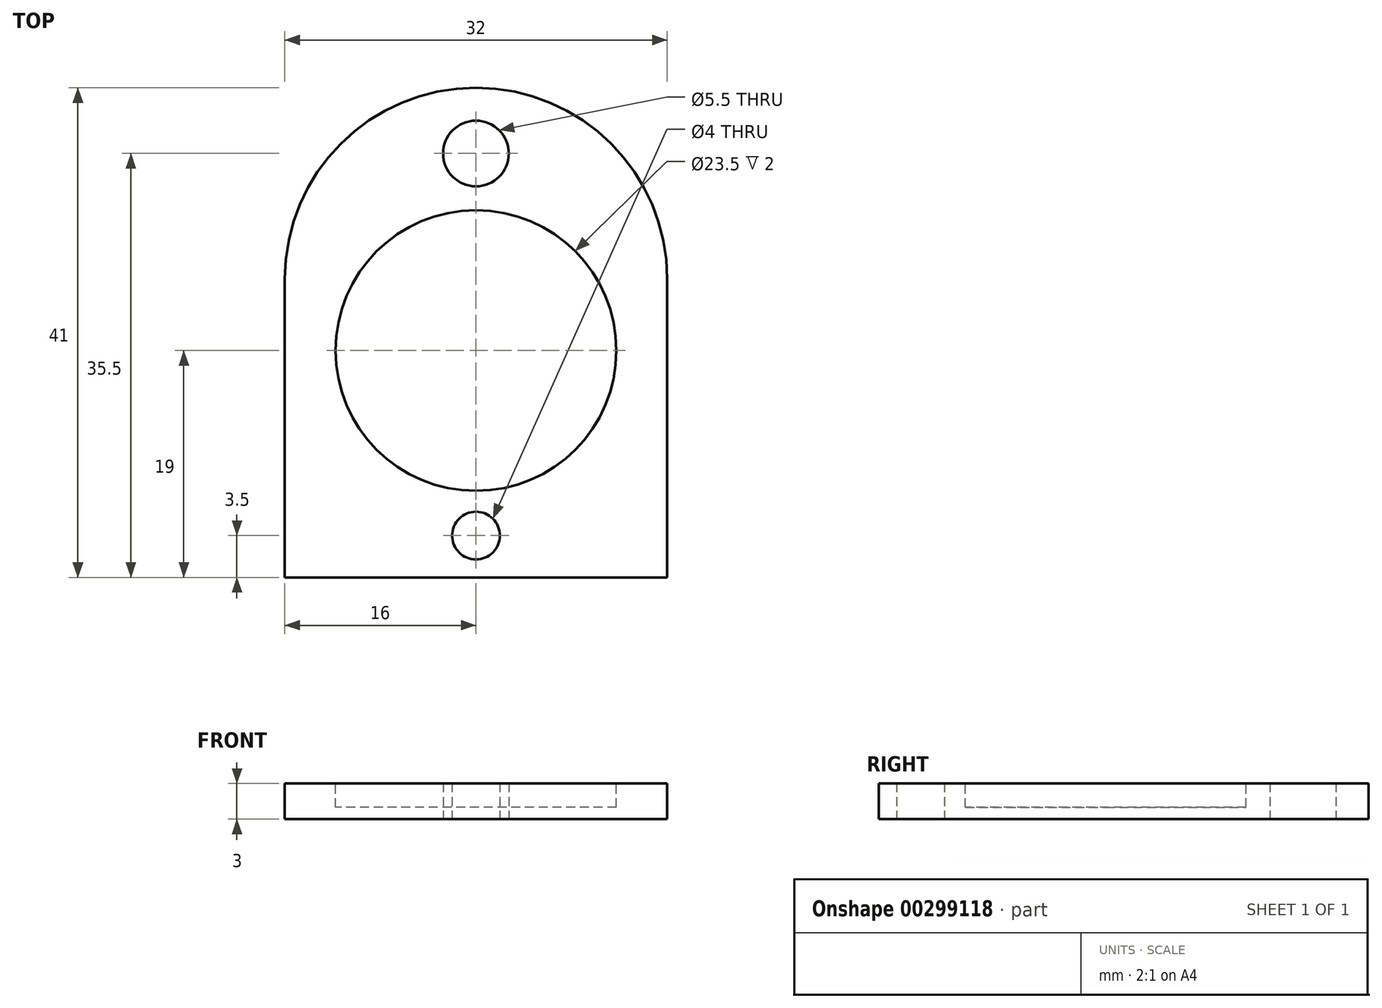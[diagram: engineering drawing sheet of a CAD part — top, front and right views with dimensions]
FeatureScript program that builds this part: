
annotation { "Feature Type Name" : "Feature", "Feature Type Description" : "" }
export const myFeature = defineFeature(function(context is Context, id is Id, definition is map)
    precondition{}
    {
        {
            var Q0;
            Q0=qCreatedBy(makeId("Top.planeOp"),FACE);
            var sketch = newSketch(context, id + "F0", { "sketchPlane" : qUnion([Q0])});
            skLineSegment(sketch, "E0.bottom", {"start": v(0, 0) * mm, "end": v(32, 0) * mm});
            skLineSegment(sketch, "E0.left", {"start": v(0, 0) * mm, "end": v(0, 25) * mm});
            skLineSegment(sketch, "E0.right", {"start": v(32, 0) * mm, "end": v(32, 25) * mm});
            skArc(sketch, "E1", {"start": v(32, 25) * mm, "mid": v(16, 41) * mm, "end": v(0, 25) * mm});
            skCircle(sketch, "E2", {"center": v(16, 35.5) * mm, "radius": 2.75 * mm});
            skCircle(sketch, "E3", {"center": v(16, 3.5) * mm, "radius": 2 * mm});
            skSolve(sketch);
        }
        {
            var Q0;
            Q0 = qSketchRegion(id + "F0", true);
            extrude(context, id + "F1", {"entities" : qUnion([Q0]), "depth" : 3 * mm});
        }
        {
            var Q0;
            Q0=makeQuery(id+"F1.opExtrude","CAP_FACE",FACE,{"disambiguationData":[OSD([sQuery(id+"F0.wireOp",EDGE,"E0.bottom"),sQuery(id+"F0.wireOp",EDGE,"E0.left"),sQuery(id+"F0.wireOp",EDGE,"E0.right"),sQuery(id+"F0.wireOp",EDGE,"E1"),sQuery(id+"F0.wireOp",EDGE,"E2"),sQuery(id+"F0.wireOp",EDGE,"E3")])],"isStart":false});
            var sketch = newSketch(context, id + "F2", { "sketchPlane" : qUnion([Q0])});
            skCircle(sketch, "E4", {"center": v(16, 19) * mm, "radius": 11.75 * mm});
            skSolve(sketch);
        }
        {
            var Q0;
            Q0 = qSketchRegion(id + "F2", true);
            extrude(context, id + "F3", {"entities" : qUnion([Q0]), "operationType" : NewBodyOperationType.REMOVE, "oppositeDirection" : true, "depth" : 2 * mm});
        }
    });
